# Revit family: Sanitary_Taps-mixers_hansgrohe_74720USA-Zesis-S-Single-lever-basin-mixer-100_CoolStart_pop-up-waste-set
name_source: partatom
category: Plumbing Fixtures
units: mm (PartAtom-declared; Revit-internal decimal feet)

## family parameters
Always vertical = No
Cut with Voids When Loaded = No
Maintain Annotation Orientation = No
OmniClass Number = 23.31.11.00
OmniClass Title = Faucets
Part Type = Normal
Room Calculation Point = No
Round Connector Dimension = Use Diameter
Shared = No
Work Plane-Based = Yes

## types (3) — shared parameters
Connector Description = Water Inlet 3/8"
Default Elevation = 0"
Description = Zesis S Single lever basin mixer 100 CoolStart with pop-up waste set
Diameter = 1/2"
Manufacturer = Hansgrohe
Model = 74720USA
Product Page URL = https://www.hansgrohe.com
Product data url = https://www.bimobject.com
URL = https://www.hansgrohe.com
Version = 1

## per-type parameters (varying)
| type | Material 1 |
| 001 Chrome | Hansgrohe - Metal - 001 Chrome |
| 671 Matt Black | Hansgrohe - Metal - 671 Matte Black |
| 821 Brushed Nickel | Hansgrohe - Metal - 821 Brushed Nickel |

## geometry (parser evidence)
native form markers: Sweep x2
no freeform markers — native parametric forms only
